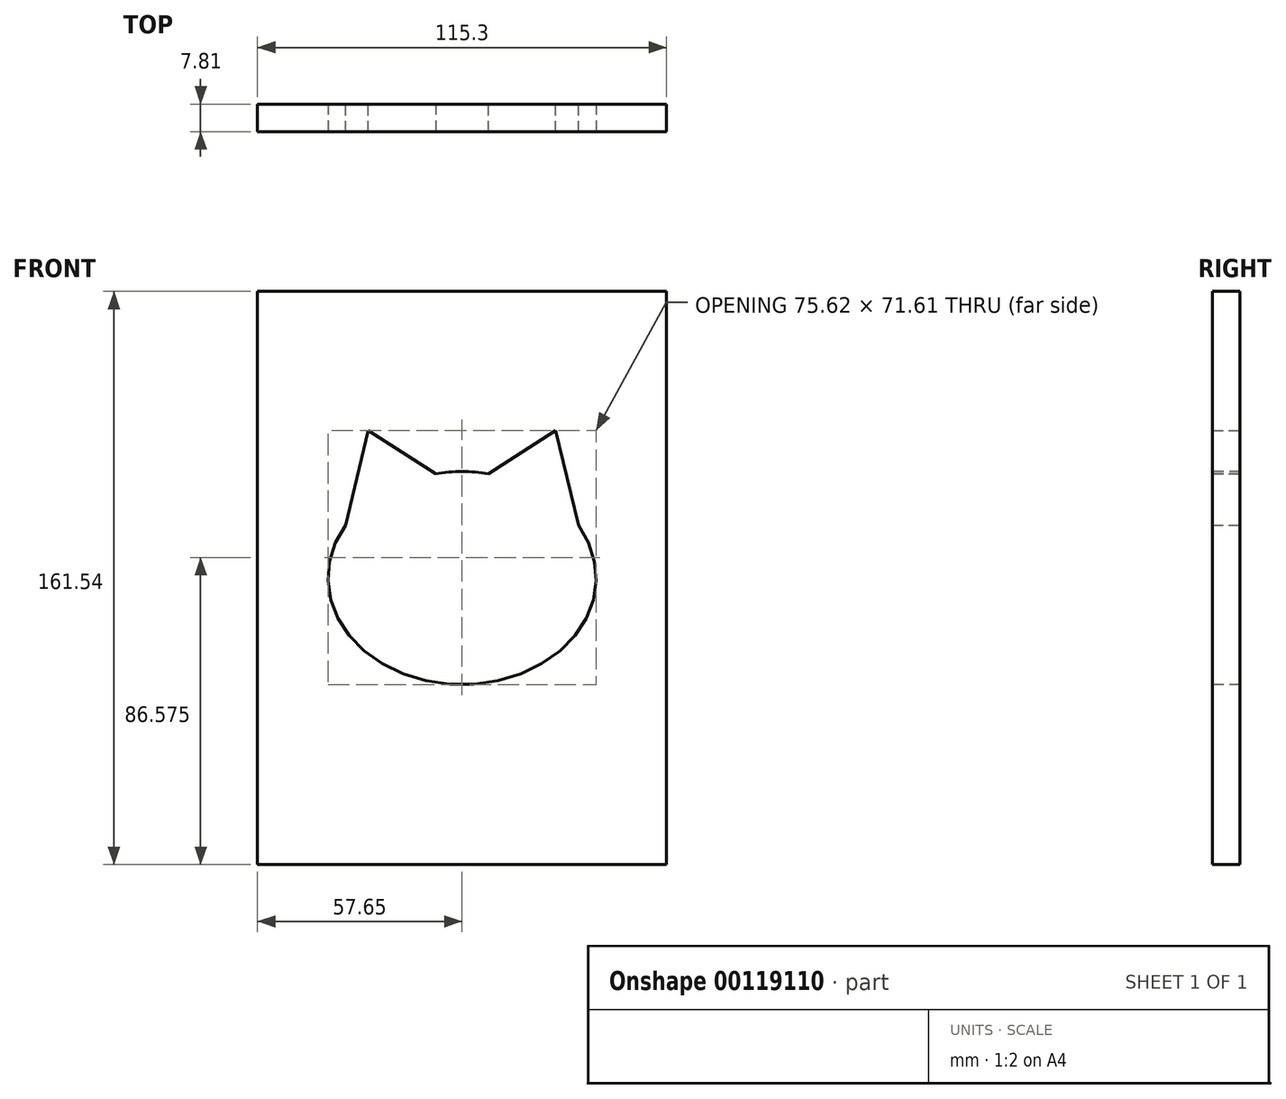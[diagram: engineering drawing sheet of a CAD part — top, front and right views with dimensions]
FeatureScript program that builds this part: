
annotation { "Feature Type Name" : "Feature", "Feature Type Description" : "" }
export const myFeature = defineFeature(function(context is Context, id is Id, definition is map)
    precondition{}
    {
        {
            var Q0;
            Q0=qCreatedBy(makeId("Front.planeOp"),FACE);
            var sketch = newSketch(context, id + "F1", { "sketchPlane" : qUnion([Q0])});
            skEllipticalArc(sketch, "E0", {});
            skLineSegment(sketch, "E1", {"start": v(-32.81, 14.9) * mm, "end": v(-26.4, 41.61) * mm});
            skLineSegment(sketch, "E2", {"start": v(-26.4, 41.61) * mm, "end": v(-7.43, 29.42) * mm});
            skLineSegment(sketch, "E3.MirrorCS", {"start": v(26.4, 41.61) * mm, "end": v(7.43, 29.42) * mm});
            skLineSegment(sketch, "E4.MirrorCS", {"start": v(32.81, 14.9) * mm, "end": v(26.4, 41.61) * mm});
            skEllipticalArc(sketch, "E5.trimOffspring", {});
            skPoint(sketch, "E6.orphan", {"position": v(0, 53.22) * mm});
            skLineSegment(sketch, "E7", {"start": v(0, 53.22) * mm, "end": v(0, 0) * mm, "construction": true});
            skLineSegment(sketch, "E8.bottom", {"start": v(57.65, -80.77) * mm, "end": v(-57.65, -80.77) * mm});
            skLineSegment(sketch, "E8.top", {"start": v(57.65, 80.77) * mm, "end": v(-57.65, 80.77) * mm});
            skLineSegment(sketch, "E8.left", {"start": v(57.65, -80.77) * mm, "end": v(57.65, 80.77) * mm});
            skLineSegment(sketch, "E8.right", {"start": v(-57.65, -80.77) * mm, "end": v(-57.65, 80.77) * mm});
            const initialGuessFJIbpNKftrgJpaaqF_0  = {"E0": [0, 0, 1, 0, 0.03781183063983917, 0.03, 2.6216164561778137, 0.5199761974119798], "E5.trimOffspring": [0, 0, 1, 0, 0.03781183063983917, 0.03, 1.37302674836442, 1.7685659052253733]};
            skSetInitialGuess(sketch, initialGuessFJIbpNKftrgJpaaqF_0);
            skSolve(sketch);
        }
        {
            var Q0;
            Q0=makeQuery(id+"F1.imprint","IMPRINT",FACE,{"disambiguationData":[TD([[makeQuery(id+"F1.imprint","IMPRINT",EDGE,{"derivedFrom":sQuery(id+"F1.wireOp",EDGE,"E0")}),-1.0]])]});
            extrude(context, id + "F0", {"entities" : qUnion([Q0]), "depth" : 7.8 * mm});
        }
    });
